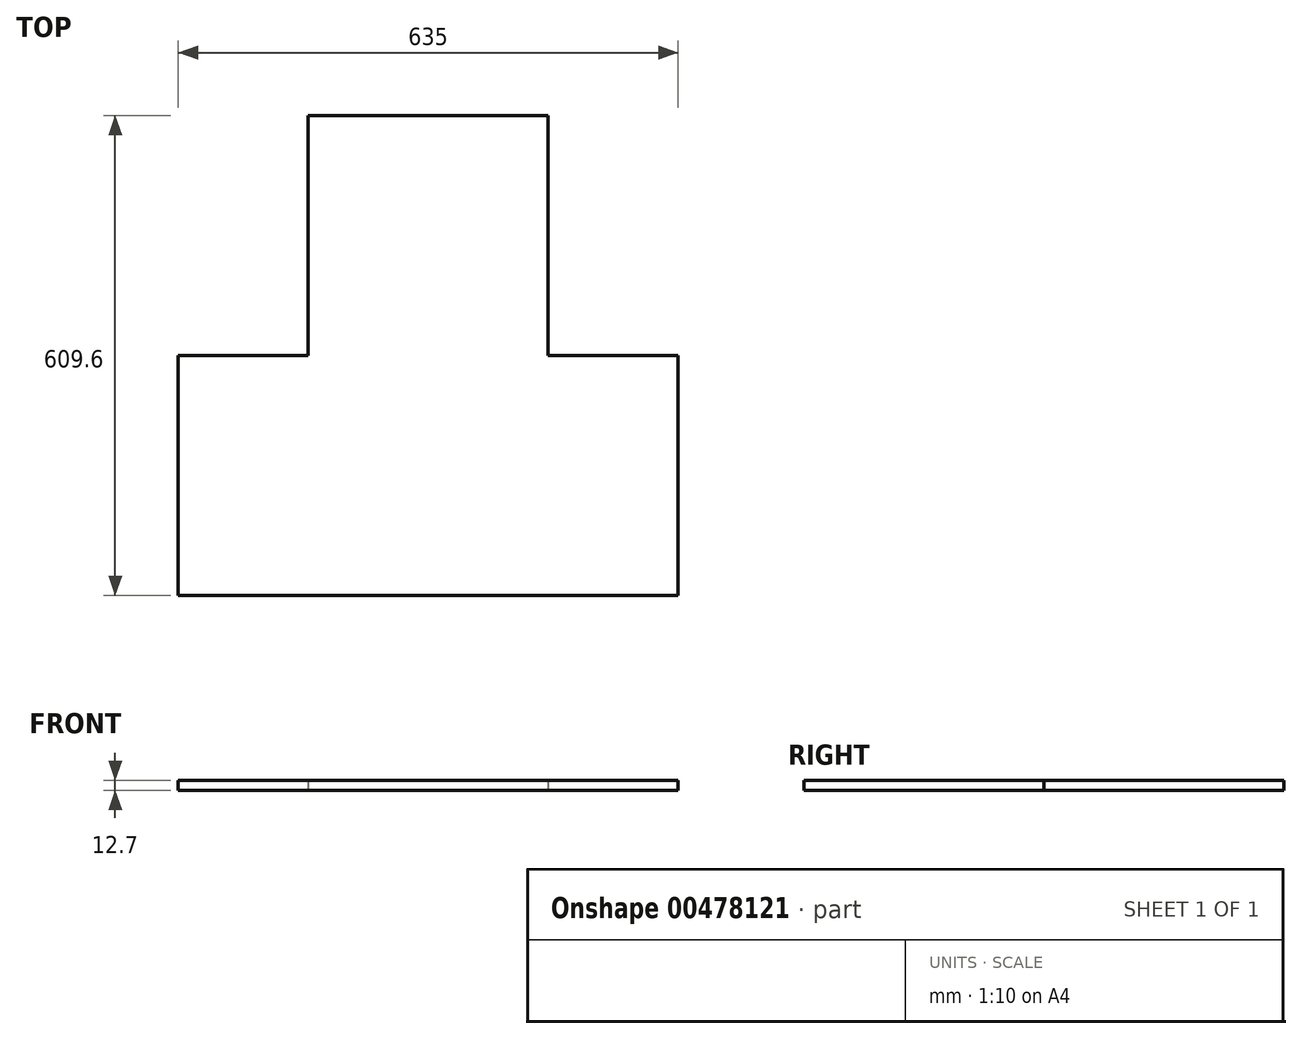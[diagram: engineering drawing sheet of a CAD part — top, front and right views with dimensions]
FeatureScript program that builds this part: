
annotation { "Feature Type Name" : "Feature", "Feature Type Description" : "" }
export const myFeature = defineFeature(function(context is Context, id is Id, definition is map)
    precondition{}
    {
        {
            var Q0;
            Q0=qCreatedBy(makeId("Top.planeOp"),FACE);
            var sketch = newSketch(context, id + "F0", { "sketchPlane" : qUnion([Q0])});
            skLineSegment(sketch, "E0.bottom", {"start": v(0, 0) * mm, "end": v(635, 0) * mm});
            skLineSegment(sketch, "E0.top", {"start": v(0, 304.8) * mm, "end": v(635, 304.8) * mm});
            skLineSegment(sketch, "E0.left", {"start": v(0, 0) * mm, "end": v(0, 304.8) * mm});
            skLineSegment(sketch, "E0.right", {"start": v(635, 0) * mm, "end": v(635, 304.8) * mm});
            skLineSegment(sketch, "E1", {"start": v(317.5, 304.8) * mm, "end": v(469.9, 304.8) * mm});
            skLineSegment(sketch, "E2.bottom", {"start": v(469.9, 304.8) * mm, "end": v(165.1, 304.8) * mm});
            skLineSegment(sketch, "E2.top", {"start": v(469.9, 609.6) * mm, "end": v(165.1, 609.6) * mm});
            skLineSegment(sketch, "E2.left", {"start": v(469.9, 304.8) * mm, "end": v(469.9, 609.6) * mm});
            skLineSegment(sketch, "E2.right", {"start": v(165.1, 304.8) * mm, "end": v(165.1, 609.6) * mm});
            skSolve(sketch);
        }
        {
            var Q0;
            Q0=makeQuery(id+"F0.imprint","IMPRINT",FACE,{"disambiguationData":[TD([[makeQuery(id+"F0.imprint","IMPRINT",EDGE,{"derivedFrom":sQuery(id+"F0.wireOp",EDGE,"E0.bottom")}),1.0]])]});
            var Q1;
            Q1=makeQuery(id+"F0.imprint","IMPRINT",FACE,{"disambiguationData":[TD([[makeQuery(id+"F0.imprint","IMPRINT",EDGE,{"derivedFrom":sQuery(id+"F0.wireOp",EDGE,"E2.top")}),1.0]])]});
            extrude(context, id + "F1", {"entities" : qUnion([Q0, Q1]), "depth" : 12.7 * mm});
        }
    });
